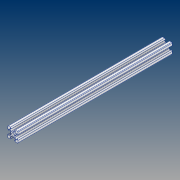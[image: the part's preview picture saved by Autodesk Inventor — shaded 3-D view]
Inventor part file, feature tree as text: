
AUTODESK INVENTOR PART (.ipt)
format: ipt  version: 2021 (Build 250183000, 183)  size: 173,056 bytes
history: native  units: mm
features: extrude x1, sketch x1
ambient origin geometry x8: Origin, YZ Plane, XZ Plane, XY Plane, X Axis, Y Axis, Z Axis, Center Point
bodies: Solid1 (feature_tree)
feature tree (2):
  extrude  "Extrusion1"  Depth=300.0mm TaperAngle=0.0deg
  sketch  "Sketch1"  dims[d1=40.0mm d2=360.0deg d3=300.0mm d4=0.0mm]
